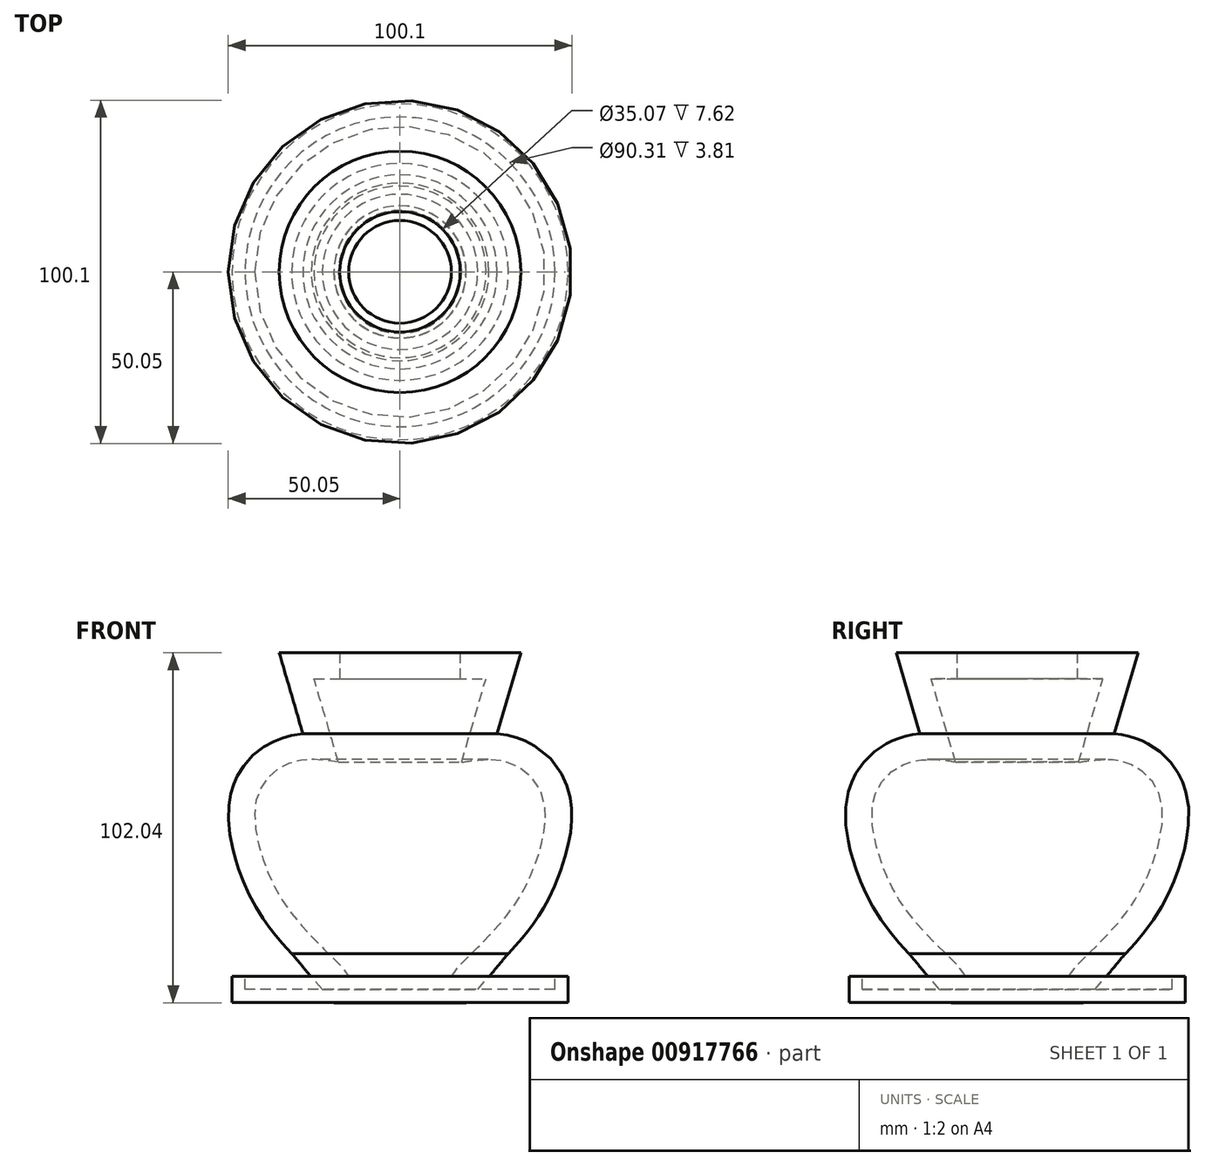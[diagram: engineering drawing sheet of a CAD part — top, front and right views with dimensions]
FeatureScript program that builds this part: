
annotation { "Feature Type Name" : "Feature", "Feature Type Description" : "" }
export const myFeature = defineFeature(function(context is Context, id is Id, definition is map)
    precondition{}
    {
        {
            var Q0;
            Q0=qCreatedBy(makeId("Front.planeOp"),FACE);
            var sketch = newSketch(context, id + "F0", { "sketchPlane" : qUnion([Q0])});
            skLineSegment(sketch, "E0", {"start": v(-17.54, 47.24) * mm, "end": v(-25.03, 47.24) * mm});
            skLineSegment(sketch, "E1", {"start": v(-25.03, 47.24) * mm, "end": v(-17.93, 22.97) * mm});
            skFitSpline(sketch, "E2", {"points": [v(-17.93, 22.97) * mm, v(-31.26, 22.97) * mm, v(-41.34, 13.78) * mm, v(-40.15, -4.6) * mm, v(-30.37, -22.7) * mm, v(-17.93, -35.7) * mm, v(-14.96, -39.56) * mm], "startDerivative": vector(-84.16, 12.29) * mm, "endDerivative": vector(47.47, -66.75) * mm});
            skLineSegment(sketch, "E3.2", {"start": v(-17.54, 54.86) * mm, "end": v(-35.2, 54.86) * mm});
            skLineSegment(sketch, "E3.3", {"start": v(-35.2, 54.86) * mm, "end": v(-28.29, 31.24) * mm});
            skFitSpline(sketch, "E3.4", {"points": [v(-16.83, 30.5) * mm, v(-17.7, 30.63) * mm, v(-19.54, 30.9) * mm, v(-22.53, 31.24) * mm, v(-25.75, 31.4) * mm, v(-28.63, 31.26) * mm, v(-31.04, 30.89) * mm, v(-32.57, 30.53) * mm, v(-33.81, 30.16) * mm, v(-35.03, 29.74) * mm, v(-36.53, 29.11) * mm, v(-38.26, 28.22) * mm, v(-40.47, 26.85) * mm, v(-43.05, 24.77) * mm, v(-45.3, 22.23) * mm, v(-46.84, 19.91) * mm, v(-47.68, 18.35) * mm, v(-48.25, 17.04) * mm, v(-48.77, 15.68) * mm, v(-49.27, 13.97) * mm, v(-49.68, 11.92) * mm, v(-50, 9.2) * mm, v(-50.01, 5.88) * mm, v(-49.6, 2) * mm, v(-48.88, -1.74) * mm, v(-48.17, -4.45) * mm, v(-47.64, -6.2) * mm, v(-47.28, -7.34) * mm, v(-46.6, -9.33) * mm, v(-45.54, -12.13) * mm, v(-44.07, -15.4) * mm, v(-42.4, -18.63) * mm, v(-40.82, -21.25) * mm, v(-39.44, -23.32) * mm, v(-38.35, -24.85) * mm, v(-37.2, -26.37) * mm, v(-35.99, -27.88) * mm, v(-34.73, -29.36) * mm, v(-33.04, -31.27) * mm, v(-30.9, -33.55) * mm, v(-28.44, -36.04) * mm, v(-26.22, -38.22) * mm, v(-24.7, -39.7) * mm, v(-23.9, -40.5) * mm, v(-23.53, -40.87) * mm, v(-23.25, -41.17) * mm, v(-23.02, -41.42) * mm, v(-22.87, -41.6) * mm, v(-22.69, -41.84) * mm, v(-22.37, -42.28) * mm, v(-21.88, -42.98) * mm, v(-21.43, -43.61) * mm, v(-21.17, -43.98) * mm]});
            skLineSegment(sketch, "E4", {"start": v(-17.54, 54.86) * mm, "end": v(-17.54, 47.24) * mm});
            skLineSegment(sketch, "E5", {"start": v(0, -44.13) * mm, "end": v(0, -47.18) * mm});
            skLineSegment(sketch, "E6", {"start": v(-14.96, -39.56) * mm, "end": v(0, -39.56) * mm});
            skLineSegment(sketch, "E7", {"start": v(0, -39.56) * mm, "end": v(0, -44.13) * mm});
            skFitSpline(sketch, "E8", {"points": [v(-32.63, -31.7) * mm, v(-25.89, -39.56) * mm], "startDerivative": vector(9.82, -10.51) * mm, "endDerivative": vector(6.94, -7.62) * mm});
            skLineSegment(sketch, "E9", {"start": v(0, -39.56) * mm, "end": v(0, 55.9) * mm, "construction": true});
            skLineSegment(sketch, "E10", {"start": v(-25.89, -39.56) * mm, "end": v(-19.23, -47.18) * mm});
            skLineSegment(sketch, "E11", {"start": v(-14.96, -39.56) * mm, "end": v(-8.76, -47.18) * mm});
            skLineSegment(sketch, "E12", {"start": v(-19.23, -47.18) * mm, "end": v(0, -47.18) * mm});
            skLineSegment(sketch, "E13", {"start": v(-25.89, -39.56) * mm, "end": v(0, -39.56) * mm});
            skSolve(sketch);
        }
        {
            var Q0;
            Q0=qCreatedBy(makeId("Front.planeOp"),FACE);
            var sketch = newSketch(context, id + "F1", { "sketchPlane" : qUnion([Q0])});
            skLineSegment(sketch, "E14", {"start": v(-48.97, -39.48) * mm, "end": v(-48.97, -47.1) * mm});
            skLineSegment(sketch, "E15", {"start": v(-48.97, -47.1) * mm, "end": v(0, -47.1) * mm});
            skLineSegment(sketch, "E16", {"start": v(-45.16, -39.48) * mm, "end": v(-45.16, -43.3) * mm});
            skLineSegment(sketch, "E17", {"start": v(-45.16, -43.3) * mm, "end": v(0, -43.3) * mm});
            skLineSegment(sketch, "E18", {"start": v(-45.16, -39.48) * mm, "end": v(-48.28, -39.48) * mm});
            skLineSegment(sketch, "E19", {"start": v(-45.16, -39.48) * mm, "end": v(-48.97, -39.48) * mm});
            skLineSegment(sketch, "E20", {"start": v(0, -43.3) * mm, "end": v(0, -47.1) * mm});
            skSolve(sketch);
        }
        {
            var Q0;
            Q0 = qSketchRegion(id + "F0", true);
            var Q1;
            Q1=sQuery(id+"F0.wireOp",EDGE,"E9");
            revolve(context, id + "F2", {"surfaceOperationType" : NewSurfaceOperationType.NEW, "entities" : qUnion([Q0]), "axis" : qUnion([Q1]), "revolveType" : RevolveType.FULL});
        }
        {
            var Q0;
            Q0 = qSketchRegion(id + "F1", true);
            var Q1;
            Q1=sQuery(id+"F0.wireOp",EDGE,"E7");
            revolve(context, id + "F3", {"operationType" : NewBodyOperationType.ADD, "surfaceOperationType" : NewSurfaceOperationType.NEW, "entities" : qUnion([Q0]), "axis" : qUnion([Q1]), "revolveType" : RevolveType.FULL});
        }
    });
